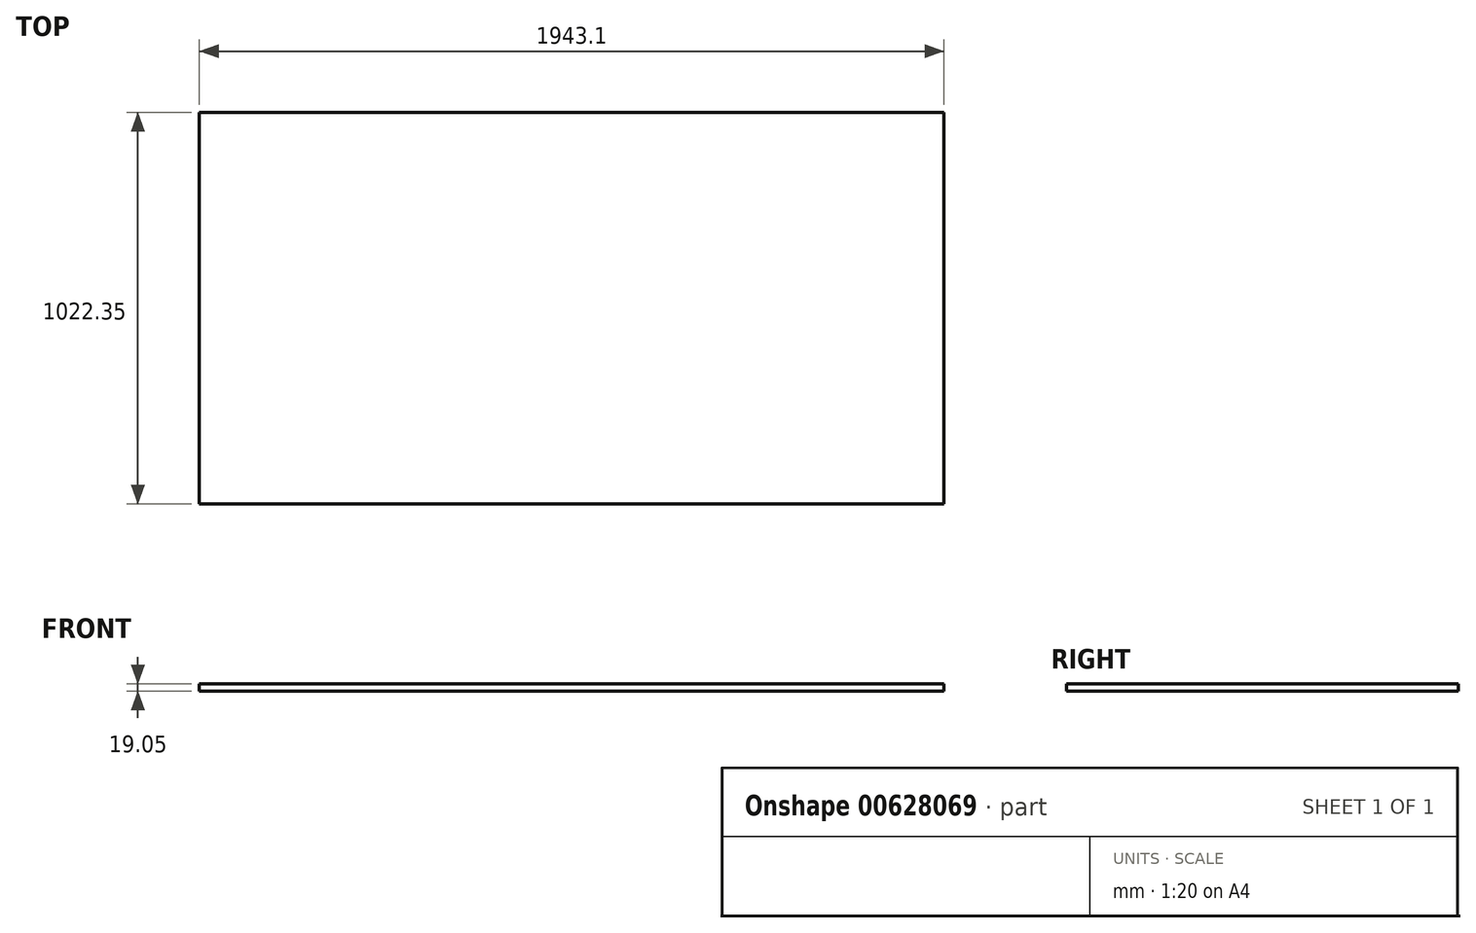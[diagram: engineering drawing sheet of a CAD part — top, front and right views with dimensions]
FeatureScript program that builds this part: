
annotation { "Feature Type Name" : "Feature", "Feature Type Description" : "" }
export const myFeature = defineFeature(function(context is Context, id is Id, definition is map)
    precondition{}
    {
        {
            var Q0;
            Q0=qCreatedBy(makeId("Top.planeOp"),FACE);
            var sketch = newSketch(context, id + "F0", { "sketchPlane" : qUnion([Q0])});
            skLineSegment(sketch, "E0.bottom", {"start": v(-1113.5, 515.64) * mm, "end": v(829.6, 515.64) * mm});
            skLineSegment(sketch, "E0.top", {"start": v(-1113.5, -506.71) * mm, "end": v(829.6, -506.71) * mm});
            skLineSegment(sketch, "E0.left", {"start": v(-1113.5, 515.64) * mm, "end": v(-1113.5, -506.71) * mm});
            skLineSegment(sketch, "E0.right", {"start": v(829.6, 515.64) * mm, "end": v(829.6, -506.71) * mm});
            skSolve(sketch);
        }
        {
            var Q0;
            Q0 = qSketchRegion(id + "F0", true);
            extrude(context, id + "F1", {"entities" : qUnion([Q0]), "depth" : 19.05 * mm, "offsetDistance" : 25.4 * mm});
        }
    });
